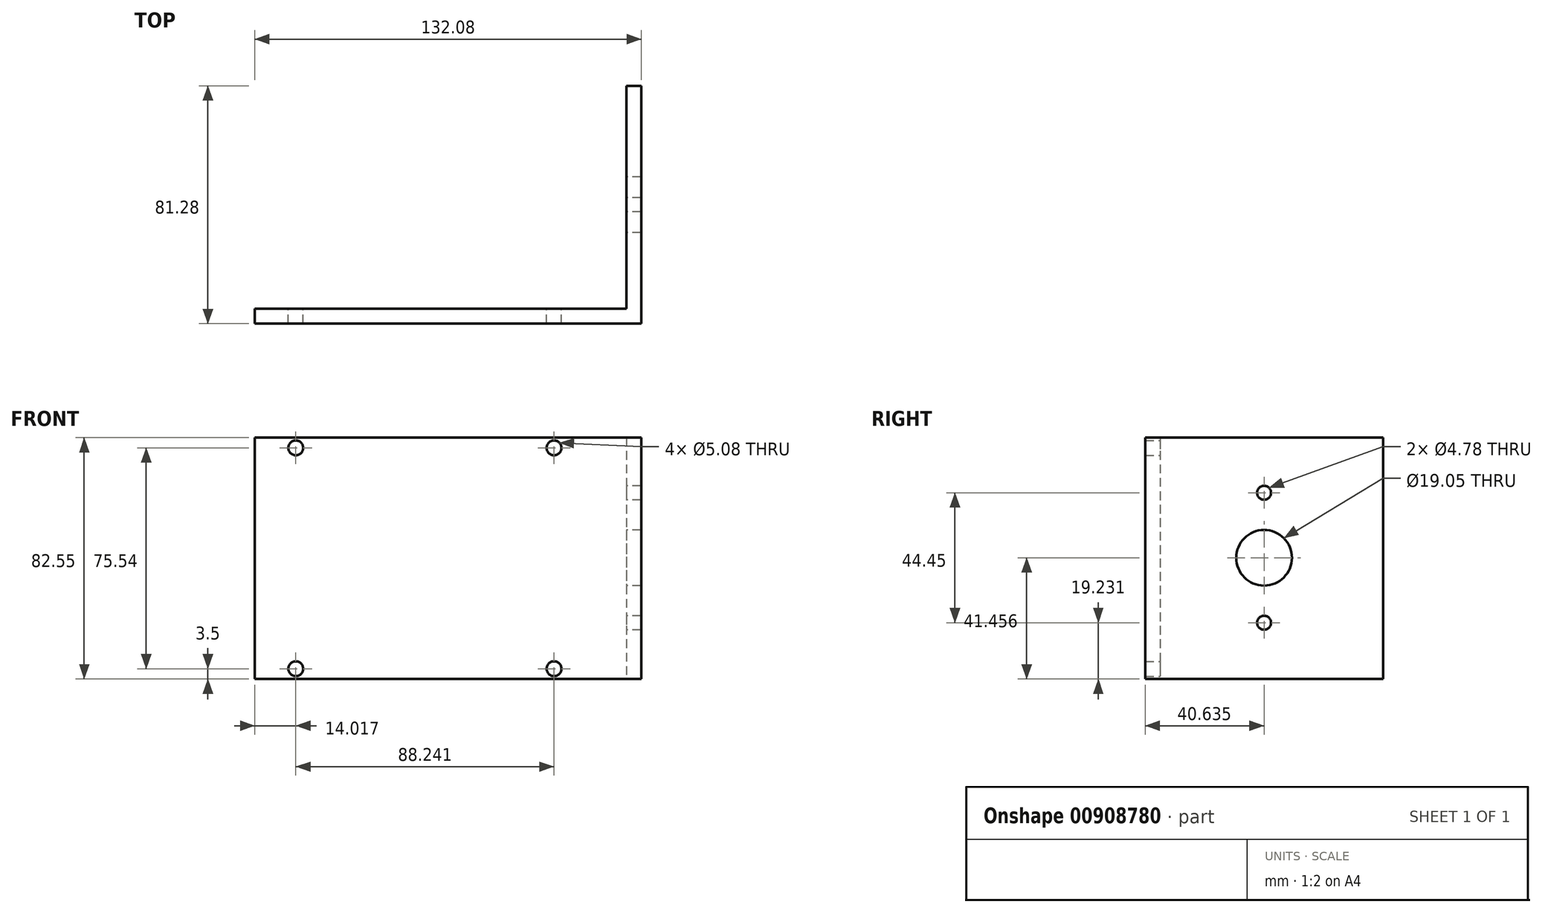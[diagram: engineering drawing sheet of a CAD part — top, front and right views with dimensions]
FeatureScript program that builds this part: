
annotation { "Feature Type Name" : "Feature", "Feature Type Description" : "" }
export const myFeature = defineFeature(function(context is Context, id is Id, definition is map)
    precondition{}
    {
        {
            var Q0;
            Q0=qCreatedBy(makeId("Top.planeOp"),FACE);
            var sketch = newSketch(context, id + "F0", { "sketchPlane" : qUnion([Q0])});
            skLineSegment(sketch, "E0", {"start": v(-68.98, -51.5) * mm, "end": v(58.02, -51.5) * mm});
            skLineSegment(sketch, "E1", {"start": v(58.02, -51.5) * mm, "end": v(58.02, 24.7) * mm});
            skLineSegment(sketch, "E2", {"start": v(-68.98, -51.5) * mm, "end": v(-68.98, -56.59) * mm});
            skLineSegment(sketch, "E3", {"start": v(-68.98, -56.59) * mm, "end": v(63.1, -56.59) * mm});
            skLineSegment(sketch, "E4", {"start": v(63.1, -56.59) * mm, "end": v(63.1, 24.7) * mm});
            skLineSegment(sketch, "E5", {"start": v(63.1, 24.7) * mm, "end": v(58.02, 24.7) * mm});
            skSolve(sketch);
        }
        {
            var Q0;
            Q0=makeQuery(id+"F0.imprint","IMPRINT",FACE,{"disambiguationData":[TD([[makeQuery(id+"F0.imprint","IMPRINT",EDGE,{"derivedFrom":sQuery(id+"F0.wireOp",EDGE,"E0")}),-1.0]])]});
            extrude(context, id + "F1", {"entities" : qUnion([Q0]), "depth" : 82.55 * mm, "offsetDistance" : 25.4 * mm});
        }
        {
            var Q0;
            Q0=makeQuery(id+"F1.opExtrude","SWEPT_FACE",FACE,{"disambiguationData":[OSD([sQuery(id+"F0.wireOp",EDGE,"E1")])]});
            var sketch = newSketch(context, id + "F2", { "sketchPlane" : qUnion([Q0])});
            skCircle(sketch, "E6", {"center": v(15.96, 41.46) * mm, "radius": 9.53 * mm});
            skLineSegment(sketch, "E7", {"start": v(15.96, 50.98) * mm, "end": v(15.96, 63.68) * mm});
            skCircle(sketch, "E8", {"center": v(15.96, 63.68) * mm, "radius": 2.38 * mm});
            skLineSegment(sketch, "E9", {"start": v(15.96, 31.93) * mm, "end": v(15.96, 19.23) * mm});
            skCircle(sketch, "E10", {"center": v(15.96, 19.23) * mm, "radius": 2.38 * mm});
            skSolve(sketch);
        }
        {
            var Q0;
            Q0=sQuery(id+"F2.wireOp",VERTEX,"E6.center");
            var Q1;
            Q1=makeQuery(id+"F1.opExtrude","SWEPT_BODY",BODY,{"disambiguationData":[OSD([sQuery(id+"F0.wireOp",EDGE,"E0"),sQuery(id+"F0.wireOp",EDGE,"E1"),sQuery(id+"F0.wireOp",EDGE,"E2"),sQuery(id+"F0.wireOp",EDGE,"E3"),sQuery(id+"F0.wireOp",EDGE,"E4"),sQuery(id+"F0.wireOp",EDGE,"E5")])]});
            hole(context, id + "F3", {"style" : HoleStyle.SIMPLE, "endStyle" : HoleEndStyle.THROUGH, "holeDiameter" : 19.05 * mm, "majorDiameter" : 6.35 * mm, "isTappedThrough" : true, "tappedDepth" : 12.7 * mm, "tapClearance" : 3, "locations" : qUnion([Q0]), "scope" : qUnion([Q1])});
        }
        {
            var Q0;
            Q0=sQuery(id+"F2.wireOp",VERTEX,"E7.end");
            var Q1;
            Q1=makeQuery(id+"F1.opExtrude","SWEPT_BODY",BODY,{"disambiguationData":[OSD([sQuery(id+"F0.wireOp",EDGE,"E0"),sQuery(id+"F0.wireOp",EDGE,"E1"),sQuery(id+"F0.wireOp",EDGE,"E2"),sQuery(id+"F0.wireOp",EDGE,"E3"),sQuery(id+"F0.wireOp",EDGE,"E4"),sQuery(id+"F0.wireOp",EDGE,"E5")])]});
            hole(context, id + "F4", {"style" : HoleStyle.SIMPLE, "endStyle" : HoleEndStyle.THROUGH, "holeDiameter" : 4.78 * mm, "majorDiameter" : 6.35 * mm, "isTappedThrough" : true, "tappedDepth" : 12.7 * mm, "tapClearance" : 3, "locations" : qUnion([Q0]), "scope" : qUnion([Q1])});
        }
        {
            var Q0;
            Q0=sQuery(id+"F2.wireOp",VERTEX,"E9.end");
            var Q1;
            Q1=makeQuery(id+"F1.opExtrude","SWEPT_BODY",BODY,{"disambiguationData":[OSD([sQuery(id+"F0.wireOp",EDGE,"E0"),sQuery(id+"F0.wireOp",EDGE,"E1"),sQuery(id+"F0.wireOp",EDGE,"E2"),sQuery(id+"F0.wireOp",EDGE,"E3"),sQuery(id+"F0.wireOp",EDGE,"E4"),sQuery(id+"F0.wireOp",EDGE,"E5")])]});
            hole(context, id + "F5", {"style" : HoleStyle.SIMPLE, "endStyle" : HoleEndStyle.THROUGH, "holeDiameter" : 4.78 * mm, "majorDiameter" : 6.35 * mm, "isTappedThrough" : true, "tappedDepth" : 12.7 * mm, "tapClearance" : 3, "locations" : qUnion([Q0]), "scope" : qUnion([Q1])});
        }
        {
            var Q0;
            Q0=makeQuery(id+"F1.opExtrude","SWEPT_FACE",FACE,{"disambiguationData":[OSD([sQuery(id+"F0.wireOp",EDGE,"E0")])]});
            var sketch = newSketch(context, id + "F6", { "sketchPlane" : qUnion([Q0])});
            skCircle(sketch, "E11", {"center": v(54.96, 3.5) * mm, "radius": 2.54 * mm});
            skLineSegment(sketch, "E12", {"start": v(54.96, 3.5) * mm, "end": v(-33.28, 3.5) * mm});
            skCircle(sketch, "E13", {"center": v(-33.28, 3.5) * mm, "radius": 2.54 * mm});
            skLineSegment(sketch, "E14", {"start": v(-33.28, 3.5) * mm, "end": v(-33.28, 79.04) * mm});
            skLineSegment(sketch, "E15", {"start": v(54.96, 3.5) * mm, "end": v(54.96, 79.04) * mm});
            skCircle(sketch, "E16", {"center": v(-33.28, 79.04) * mm, "radius": 2.54 * mm});
            skCircle(sketch, "E17", {"center": v(54.96, 79.04) * mm, "radius": 2.54 * mm});
            skSolve(sketch);
        }
        {
            var Q0;
            Q0=sQuery(id+"F6.wireOp",VERTEX,"E14.end");
            var Q1;
            Q1=sQuery(id+"F6.wireOp",VERTEX,"E15.end");
            var Q2;
            Q2=sQuery(id+"F6.wireOp",VERTEX,"E12.start");
            var Q3;
            Q3=sQuery(id+"F6.wireOp",VERTEX,"E12.end");
            var Q4;
            Q4=makeQuery(id+"F1.opExtrude","SWEPT_BODY",BODY,{"disambiguationData":[OSD([sQuery(id+"F0.wireOp",EDGE,"E0"),sQuery(id+"F0.wireOp",EDGE,"E1"),sQuery(id+"F0.wireOp",EDGE,"E2"),sQuery(id+"F0.wireOp",EDGE,"E3"),sQuery(id+"F0.wireOp",EDGE,"E4"),sQuery(id+"F0.wireOp",EDGE,"E5")])]});
            hole(context, id + "F7", {"style" : HoleStyle.SIMPLE, "endStyle" : HoleEndStyle.THROUGH, "holeDiameter" : 5.08 * mm, "majorDiameter" : 6.35 * mm, "isTappedThrough" : true, "tappedDepth" : 12.7 * mm, "tapClearance" : 3, "locations" : qUnion([Q0, Q1, Q2, Q3]), "scope" : qUnion([Q4])});
        }
    });
